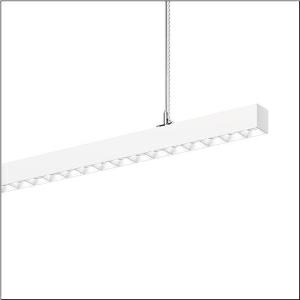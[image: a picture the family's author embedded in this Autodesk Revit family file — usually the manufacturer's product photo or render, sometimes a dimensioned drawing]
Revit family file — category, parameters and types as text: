
# Revit family: silica_r__21_51mx36dc3dwb_b05b
name_source: partatom
category: Lighting Fixtures
units: mm (PartAtom-declared; Revit-internal decimal feet)

## family parameters
Cut with Voids When Loaded = No
Host = Face
Light Source = No
Part Type = Normal
Room Calculation Point = No
Round Connector Dimension = Use Diameter
Shared = No

## types (1)
- --- (1 x LED, 17650 lm, 104.1 W, 3000K)
    Apparent Load = 104 VA
    CIE Flux Codes = 83 98 100 61 100
    Color Rendering = 80
    Color Temperature = 3000K
    Default Elevation = 1800 mm
    Description = Silica® 21, office luminaire, primary light control with darklight reflector, of PMMA, white, CAT 2 (L<= 3000cd/m²), light emission: direct/indirect distribution, primary light characteristic: symmetric, installation type: suspended mounting, LED, rated luminous flux: 17.650lm, luminous efficacy: 170lm/W, light colour: 830, colour temperature: 3000K, with terminal, 3+2-pole, max. 2.5mm², mains connection: 220..240V, AC, 50/60Hz, rated input power: 104.1W, luminaire housing, of aluminium, traffic white (RAL 9016), length: 3.004mm, width: 53mm, height: 53mm, protection rating (complete): IP20, insulation class (complete): insulation class I (protective earthing), certification: CE, permissible operating ambient temperature: 0..+35°C, standard: EN 50419, packaging unit: 1 piece
    Height = 53 mm
    Lamp = 1 x LED
    Lamp Light Flux = 17650 lm
    Lamp Power = 104.1 W
    Lamp count = 1
    Length = 3004 mm
    Luminous efficacy = 170 lm/W
    Manufacturer = Siteco
    ModVariant = No
    Model = 51MX36DC3DWB
    Mounting Place = Ceiling
    Mounting Type = Pendant
    Number of Poles = 1
    OnlyDefault = Yes
    Power Factor = 1
    Product Name = Silica® 21
    Product group = office luminaire | ceiling pendant
    ProductGroupID = 902
    Protection Class = Protection class I
    Protection Degree = IP 20
    RLX_Detail_Level = 1
    RLX_Emergency_Light_Flux = 0 lm
    RLX_Emergency_Type = 0
    RLX_Emergency_Type_DB = No
    RlxData = <blob elided: 61733 chars, md5=0d187327>
    Socket = socket
    Standby Power = 0 W
    System Light Flux = 17650 lm
    System Power = 104 W
    Type Comments = factory setting: luminous flux: 100 % | dim-lin: 254 | 359 mA
    Type Image = l_1313634.jpg
    URL = http://relux.com
    VarID = @adj_070291
    Voltage = 0 V
    Weight = 0.00 kg
    Width = 53 mm

## geometry (parser evidence)
native form markers: Blend x4, Sweep x11
no freeform markers — native parametric forms only
